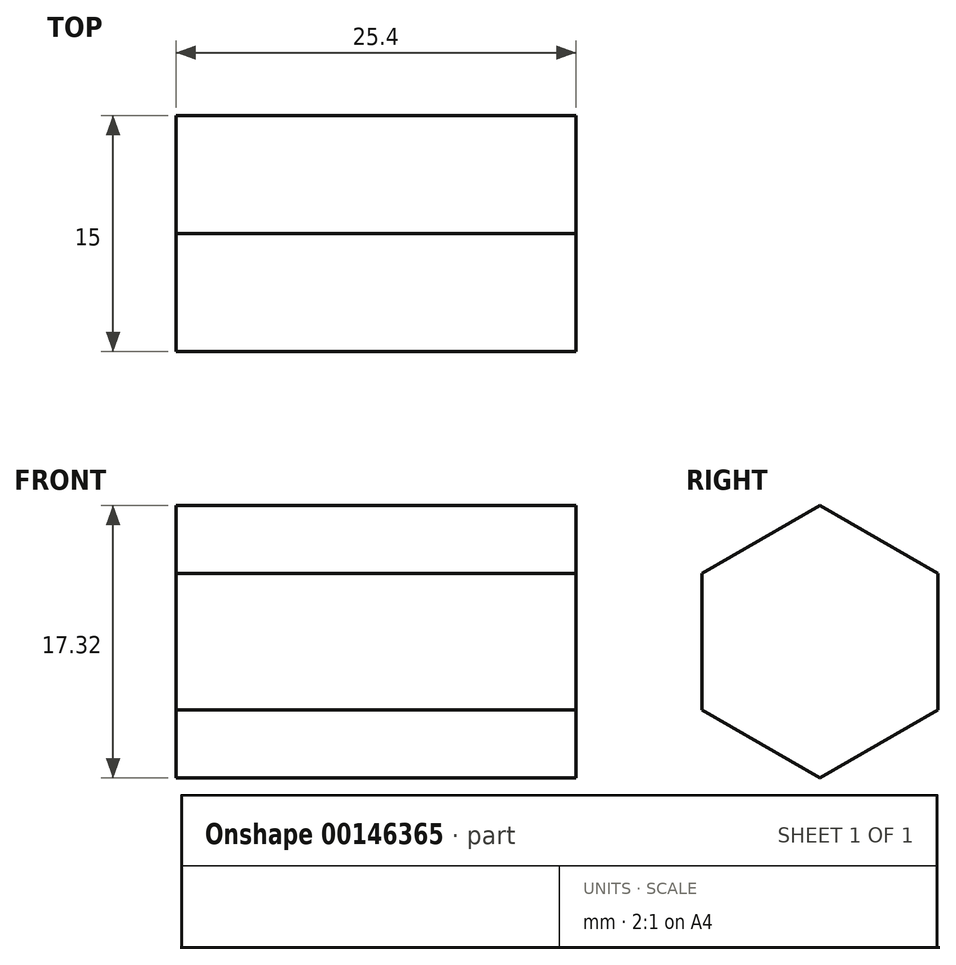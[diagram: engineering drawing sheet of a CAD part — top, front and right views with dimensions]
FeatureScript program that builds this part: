
annotation { "Feature Type Name" : "Feature", "Feature Type Description" : "" }
export const myFeature = defineFeature(function(context is Context, id is Id, definition is map)
    precondition{}
    {
        {
            var Q0;
            Q0=qCreatedBy(makeId("Right.planeOp"),FACE);
            var sketch = newSketch(context, id + "F0", { "sketchPlane" : qUnion([Q0])});
            skCircle(sketch, "E0.cCircle", {"center": v(0, 0) * mm, "radius": 7.5 * mm, "construction": true});
            skLineSegment(sketch, "E0.0", {"start": v(7.5, 4.33) * mm, "end": v(7.5, -4.33) * mm});
            skLineSegment(sketch, "E0.1", {"start": v(7.5, -4.33) * mm, "end": v(0, -8.66) * mm});
            skLineSegment(sketch, "E0.2", {"start": v(0, -8.66) * mm, "end": v(-7.5, -4.33) * mm});
            skLineSegment(sketch, "E0.3", {"start": v(-7.5, -4.33) * mm, "end": v(-7.5, 4.33) * mm});
            skLineSegment(sketch, "E0.4", {"start": v(-7.5, 4.33) * mm, "end": v(0, 8.66) * mm});
            skLineSegment(sketch, "E0.5", {"start": v(0, 8.66) * mm, "end": v(7.5, 4.33) * mm});
            skPoint(sketch, "E0.0.midPoint", {"position": v(7.5, 0) * mm});
            skSolve(sketch);
        }
        {
            var Q0;
            Q0 = qSketchRegion(id + "F0", true);
            extrude(context, id + "F1", {"entities" : qUnion([Q0]), "depth" : 25.4 * mm});
        }
    });
